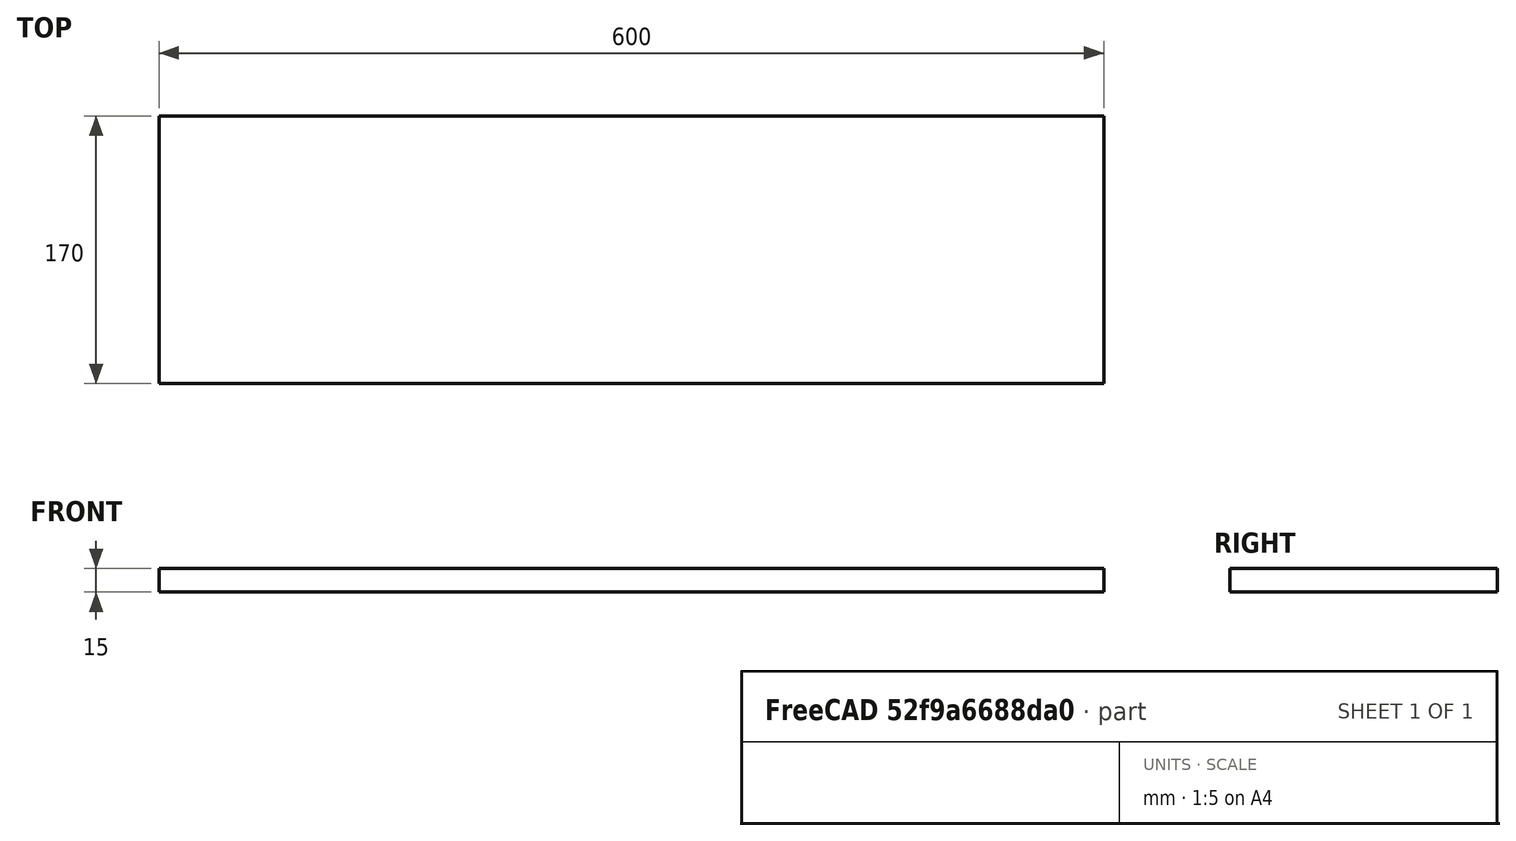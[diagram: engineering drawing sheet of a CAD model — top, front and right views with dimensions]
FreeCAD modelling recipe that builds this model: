
FCSTD DOCUMENT  (FreeCAD 1.0R39319 (Git))
Label: top
License: All rights reserved
LicenseURL: http://en.wikipedia.org/wiki/All_rights_reserved
objects: Sketcher::SketchObject×1, PartDesign::Pad×1, PartDesign::Body×1
note: 6 computed .brp shape members not serialized (recipe doc carries the construction recipe); baked Part::Feature solids carry a one-line shape summary decoded from their .brp

FEATURE [Sketcher::SketchObject] Sketch  label="top_sketch"
  ArcFitTolerance = 0
  AttachmentSupport = -> [XY_Plane]
  FullyConstrained = true
  MakeInternals = false
  MapMode = 5
  sketch-geometry (4):
    g0: LineSegment StartX=0 StartY=0 StartZ=0 EndX=600 EndY=0 EndZ=0
    g1: LineSegment StartX=600 StartY=0 StartZ=0 EndX=600 EndY=170 EndZ=0
    g2: LineSegment StartX=600 StartY=170 StartZ=0 EndX=0 EndY=170 EndZ=0
    g3: LineSegment StartX=0 StartY=170 StartZ=0 EndX=0 EndY=0 EndZ=0
  constraints (11):
    c: Coincident(g0,g1)
    c: Coincident(g1,g2)
    c: Coincident(g2,g3)
    c: Coincident(g3,g0)
    c: Horizontal(g0)
    c: Horizontal(g2)
    c: Vertical(g1)
    c: Vertical(g3)
    c: Coincident(g0,g-1)
    c: DistanceY(g3,g3) = 170
    c: DistanceX(g0,g0) = 600
FEATURE [PartDesign::Pad] Pad  label="top_pad"
  AllowMultiFace = false
  Direction = (0,0,1)
  Length = 15
  Length2 = 100
  Profile = -> Sketch
  ReferenceAxis = -> Sketch [N_Axis]
  Suppressed = false
  Type = 0
FEATURE [PartDesign::Body] Body  label="top_body"
  AllowCompound = false
  Group = -> [Sketch,Pad]
  Origin = -> Origin
  Tip = -> Pad
